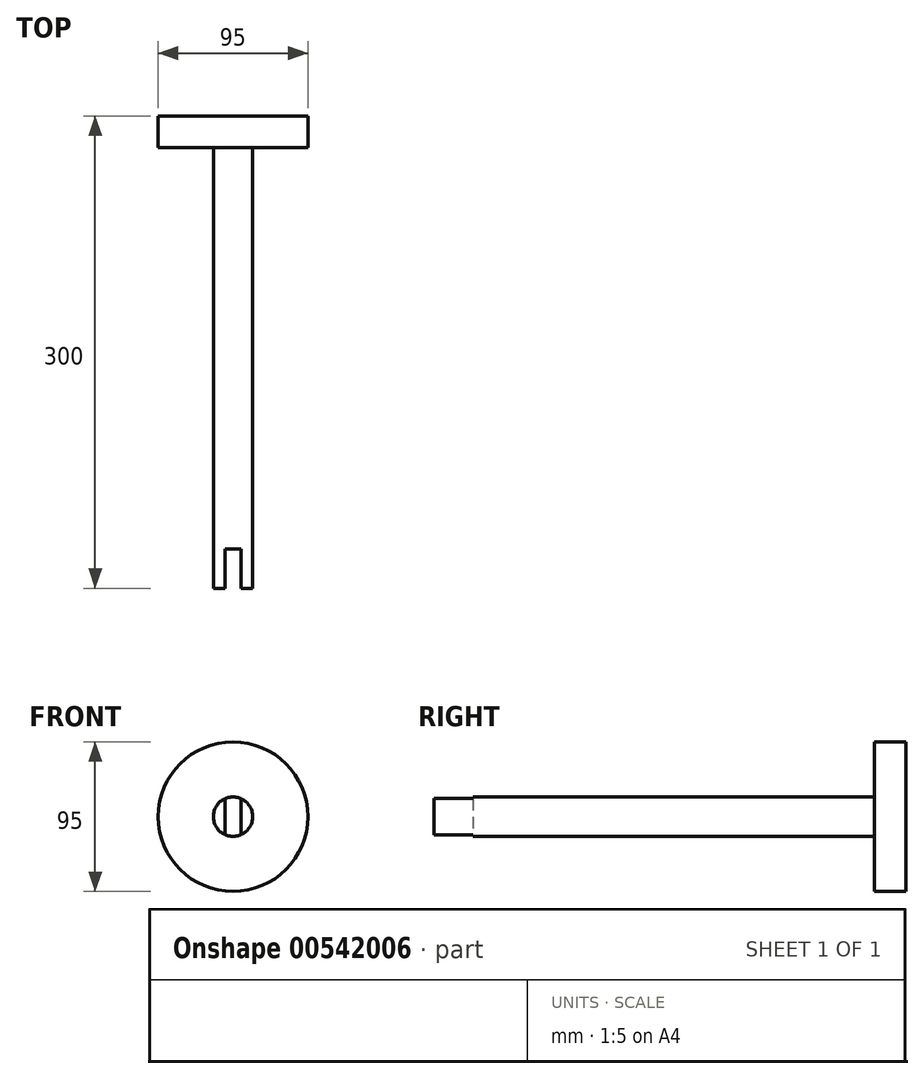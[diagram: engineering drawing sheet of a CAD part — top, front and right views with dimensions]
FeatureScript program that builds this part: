
annotation { "Feature Type Name" : "Feature", "Feature Type Description" : "" }
export const myFeature = defineFeature(function(context is Context, id is Id, definition is map)
    precondition{}
    {
        {
            var Q0;
            Q0=qCreatedBy(makeId("Front.planeOp"),FACE);
            var sketch = newSketch(context, id + "F0", { "sketchPlane" : qUnion([Q0])});
            skCircle(sketch, "E0", {"center": v(0, 0) * mm, "radius": 47.5 * mm});
            skSolve(sketch);
        }
        {
            var Q0;
            Q0=makeQuery(id+"F0.imprint","IMPRINT",FACE,{"disambiguationData":[TD([[makeQuery(id+"F0.imprint","IMPRINT",EDGE,{"derivedFrom":sQuery(id+"F0.wireOp",EDGE,"E0")}),1.0]])]});
            var Q1;
            Q1=sQuery(id+"F0.wireOp",EDGE,"E0");
            extrude(context, id + "F1", {"entities" : qUnion([Q0]), "surfaceEntities" : qUnion([Q1]), "depth" : 20 * mm, "offsetDistance" : 25 * mm});
        }
        {
            var Q0;
            Q0=makeQuery(id+"F1.opExtrude","CAP_FACE",FACE,{"disambiguationData":[OSD([sQuery(id+"F0.wireOp",EDGE,"E0")])],"isStart":false});
            var sketch = newSketch(context, id + "F2", { "sketchPlane" : qUnion([Q0])});
            skCircle(sketch, "E1", {"center": v(0, 0) * mm, "radius": 12.5 * mm});
            skSolve(sketch);
        }
        {
            var Q0;
            Q0 = qSketchRegion(id + "F2", true);
            extrude(context, id + "F3", {"entities" : qUnion([Q0]), "operationType" : NewBodyOperationType.ADD, "depth" : 280 * mm, "offsetDistance" : 25 * mm});
        }
        {
            var Q0;
            Q0=makeQuery(id+"F3.opExtrude","CAP_FACE",FACE,{"disambiguationData":[OSD([sQuery(id+"F2.wireOp",EDGE,"E1")])],"isStart":false});
            var sketch = newSketch(context, id + "F4", { "sketchPlane" : qUnion([Q0])});
            skLineSegment(sketch, "E2.bottom", {"start": v(5, 12.5) * mm, "end": v(-5, 12.5) * mm});
            skLineSegment(sketch, "E2.top", {"start": v(5, -12.5) * mm, "end": v(-5, -12.5) * mm});
            skLineSegment(sketch, "E2.left", {"start": v(5, 12.5) * mm, "end": v(5, -12.5) * mm});
            skLineSegment(sketch, "E2.right", {"start": v(-5, 12.5) * mm, "end": v(-5, -12.5) * mm});
            skPoint(sketch, "E2.middle", {"position": v(0, 0) * mm});
            skSolve(sketch);
        }
        {
            var Q0;
            Q0 = qSketchRegion(id + "F4", true);
            extrude(context, id + "F5", {"entities" : qUnion([Q0]), "operationType" : NewBodyOperationType.REMOVE, "oppositeDirection" : true, "depth" : 25 * mm, "offsetDistance" : 25 * mm});
        }
        {
            var Q0;
            Q0=makeQuery(id+"F5.boolean.opBoolean","COPY",FACE,{"derivedFrom":makeQuery(id+"F5.opExtrude","SWEPT_FACE",FACE,{"disambiguationData":[OSD([sQuery(id+"F4.wireOp",EDGE,"E2.right")])]})});
            cPlane(context, id + "F6", {"entities" : qUnion([Q0]), "cplaneType" : CPlaneType.OFFSET, "offset" : 5 * mm, "width" : 150 * mm, "height" : 150 * mm});
        }
    });
